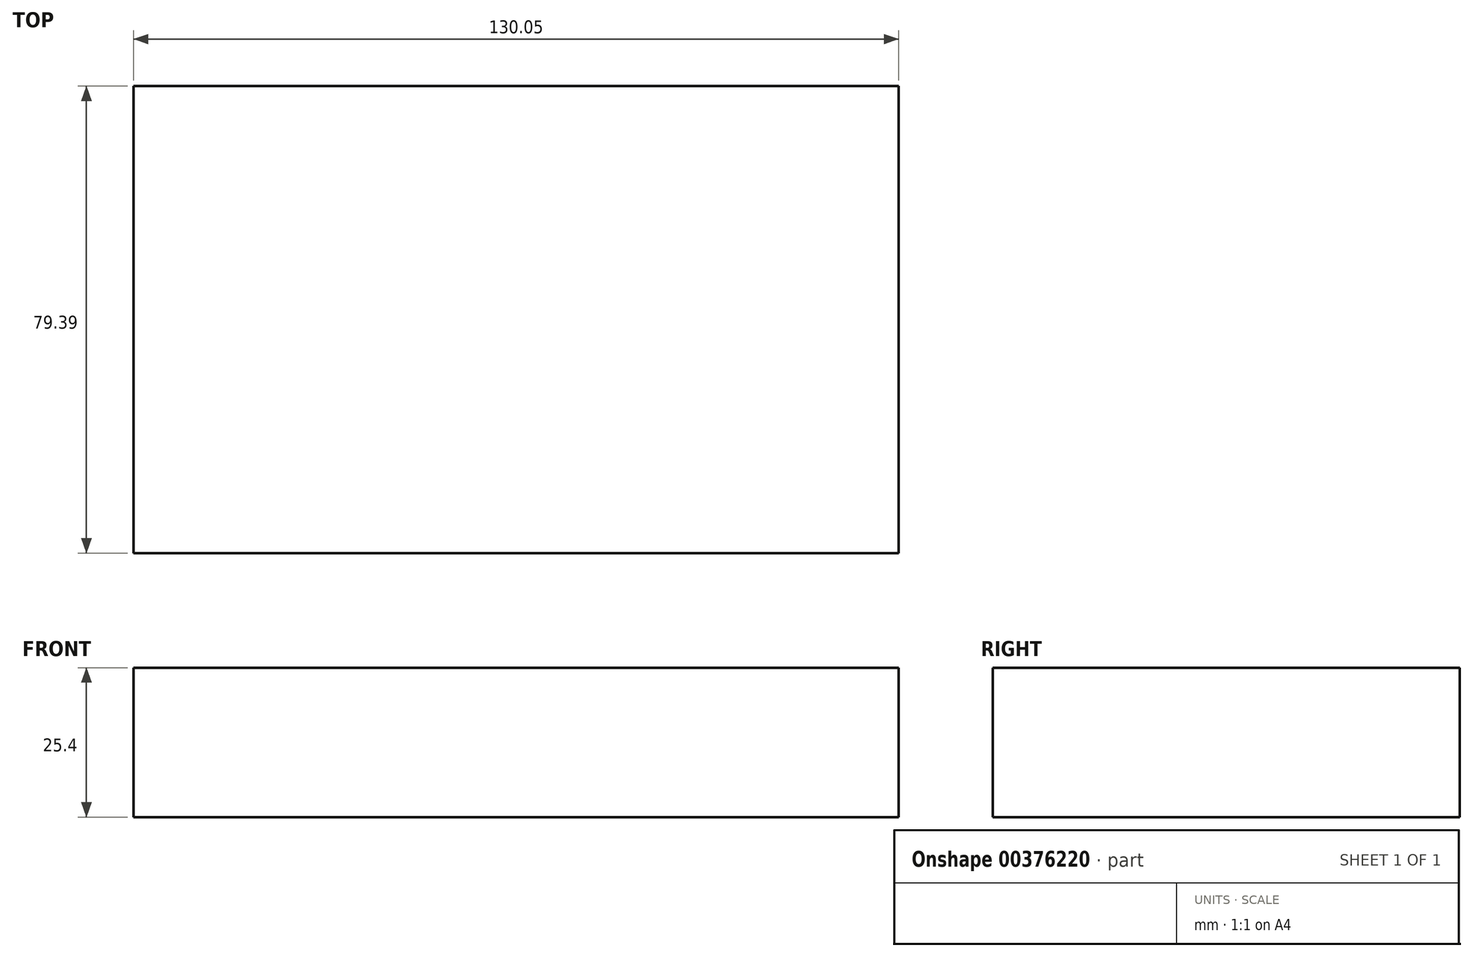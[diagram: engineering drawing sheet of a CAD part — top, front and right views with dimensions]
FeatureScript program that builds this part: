
annotation { "Feature Type Name" : "Feature", "Feature Type Description" : "" }
export const myFeature = defineFeature(function(context is Context, id is Id, definition is map)
    precondition{}
    {
        {
            var Q0;
            Q0=qCreatedBy(makeId("Top.planeOp"),FACE);
            var sketch = newSketch(context, id + "F0", { "sketchPlane" : qUnion([Q0])});
            skLineSegment(sketch, "E0.bottom", {"start": v(76.1, -34.07) * mm, "end": v(-53.94, -34.07) * mm});
            skLineSegment(sketch, "E0.top", {"start": v(76.1, 45.32) * mm, "end": v(-53.94, 45.32) * mm});
            skLineSegment(sketch, "E0.left", {"start": v(76.1, -34.07) * mm, "end": v(76.1, 45.32) * mm});
            skLineSegment(sketch, "E0.right", {"start": v(-53.94, -34.07) * mm, "end": v(-53.94, 45.32) * mm});
            skSolve(sketch);
        }
        {
            var Q0;
            Q0=makeQuery(id+"F0.imprint","IMPRINT",FACE,{"disambiguationData":[TD([[makeQuery(id+"F0.imprint","IMPRINT",EDGE,{"derivedFrom":sQuery(id+"F0.wireOp",EDGE,"E0.bottom")}),-1.0]])]});
            extrude(context, id + "F1", {"entities" : qUnion([Q0]), "depth" : 25.4 * mm});
        }
    });
